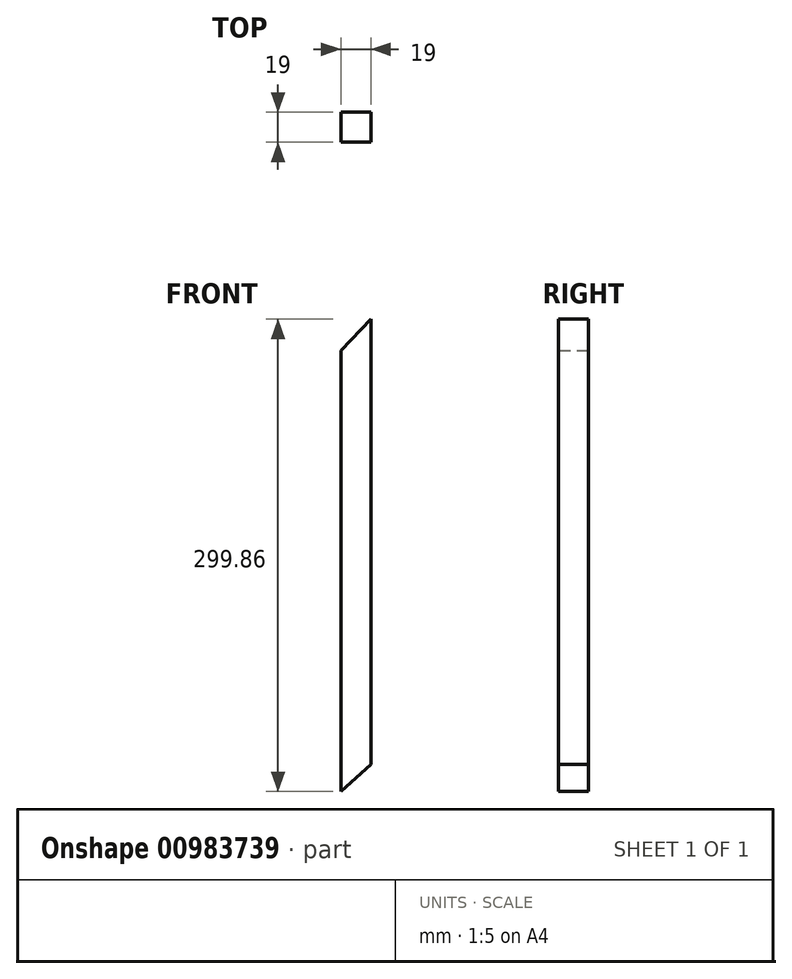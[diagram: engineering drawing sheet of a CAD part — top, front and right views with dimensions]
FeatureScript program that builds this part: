
annotation { "Feature Type Name" : "Feature", "Feature Type Description" : "" }
export const myFeature = defineFeature(function(context is Context, id is Id, definition is map)
    precondition{}
    {
        {
            var Q0;
            Q0=qCreatedBy(makeId("Front.planeOp"),FACE);
            var sketch = newSketch(context, id + "F0", { "sketchPlane" : qUnion([Q0])});
            skLineSegment(sketch, "E0.top", {"start": v(-18.85, -244.17) * mm, "end": v(0.15, -244.17) * mm});
            skLineSegment(sketch, "E0.left", {"start": v(-18.85, 35.83) * mm, "end": v(-18.85, -244.17) * mm});
            skLineSegment(sketch, "E0.right", {"start": v(0.15, 55.7) * mm, "end": v(0.15, -227.07) * mm});
            skLineSegment(sketch, "E1", {"start": v(0.15, 55.7) * mm, "end": v(-18.85, 35.83) * mm});
            skLineSegment(sketch, "E2", {"start": v(-18.85, -244.17) * mm, "end": v(0.15, -227.07) * mm});
            skSolve(sketch);
        }
        {
            var Q0;
            Q0 = qSketchRegion(id + "F0", true);
            extrude(context, id + "F1", {"entities" : qUnion([Q0]), "depth" : 19 * mm, "offsetDistance" : 25.4 * mm});
        }
    });
